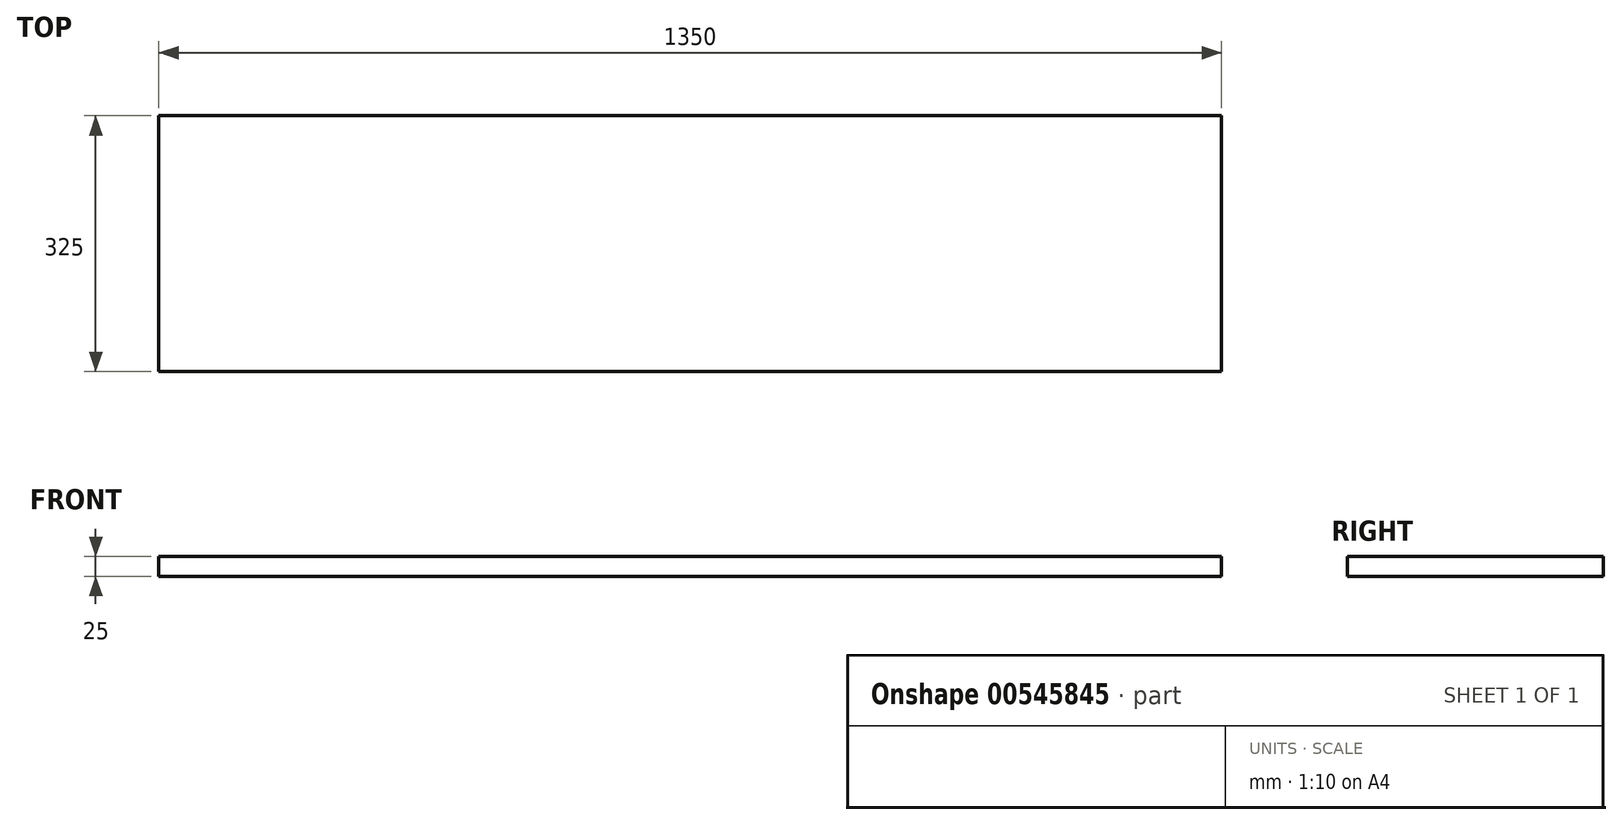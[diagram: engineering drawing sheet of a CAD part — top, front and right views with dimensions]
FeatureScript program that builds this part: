
annotation { "Feature Type Name" : "Feature", "Feature Type Description" : "" }
export const myFeature = defineFeature(function(context is Context, id is Id, definition is map)
    precondition{}
    {
        {
            var Q0;
            Q0=qCreatedBy(makeId("Top.planeOp"),FACE);
            var sketch = newSketch(context, id + "F0", { "sketchPlane" : qUnion([Q0])});
            skLineSegment(sketch, "E0", {"start": v(0, 0) * mm, "end": v(0, -1700) * mm, "construction": true});
            skLineSegment(sketch, "E1", {"start": v(-675, 0) * mm, "end": v(0, 0) * mm, "construction": true});
            skLineSegment(sketch, "E2", {"start": v(-675, -1350) * mm, "end": v(-675, -1700) * mm, "construction": true});
            skLineSegment(sketch, "E3", {"start": v(-675, -1700) * mm, "end": v(-425, -1700) * mm, "construction": true});
            skLineSegment(sketch, "E4.MirrorCS", {"start": v(675, 0) * mm, "end": v(0, 0) * mm, "construction": true});
            skLineSegment(sketch, "E5", {"start": v(-425, -1700) * mm, "end": v(-675, -1350) * mm, "construction": true});
            skLineSegment(sketch, "E6", {"start": v(675, 0) * mm, "end": v(675, -1350) * mm, "construction": true});
            skLineSegment(sketch, "E7", {"start": v(425, -1700) * mm, "end": v(-425, -1700) * mm, "construction": true});
            skLineSegment(sketch, "E8", {"start": v(675, -1350) * mm, "end": v(425, -1700) * mm, "construction": true});
            skLineSegment(sketch, "E9", {"start": v(-675, -1350) * mm, "end": v(-675, 0) * mm, "construction": true});
            skLineSegment(sketch, "E10", {"start": v(-675, -650) * mm, "end": v(675, -650) * mm});
            skLineSegment(sketch, "E11.bottom", {"start": v(-675, -325) * mm, "end": v(675, -325) * mm});
            skLineSegment(sketch, "E11.left", {"start": v(-675, -325) * mm, "end": v(-675, -650) * mm});
            skLineSegment(sketch, "E11.right", {"start": v(675, -325) * mm, "end": v(675, -650) * mm});
            skSolve(sketch);
        }
        {
            var Q0;
            Q0 = qSketchRegion(id + "F0", true);
            extrude(context, id + "F1", {"entities" : qUnion([Q0]), "depth" : 25 * mm, "offsetDistance" : 25 * mm});
        }
    });
